FCSTD DOCUMENT  (FreeCAD 0.20R28647 (Git))
Label: assembly
License: All rights reserved
LicenseURL: http://en.wikipedia.org/wiki/All_rights_reserved
objects: App::Link×4, App::DocumentObjectGroup×3, PartDesign::CoordinateSystem×1, App::FeaturePython×1, App::Part×1
note: 1 computed .brp shape members not serialized (recipe doc carries the construction recipe); baked Part::Feature solids carry a one-line shape summary decoded from their .brp
EXTERNAL_REF file=axis.FCStd obj=LCS_Origin
EXTERNAL_REF file=axis.FCStd obj=Assembly
EXTERNAL_REF file=bearing.FCStd obj=LCS_1
EXTERNAL_REF file=bearing.FCStd obj=Assembly
EXTERNAL_REF file=bearing.FCStd obj=LCS_2
EXTERNAL_REF file=axis.FCStd obj=LCS_1

FEATURE [App::DocumentObjectGroup] Parts
FEATURE [PartDesign::CoordinateSystem] LCS_Origin
  AttacherType = Attacher::AttachEngine3D
  MapMode = 2
  Support = -> [X_Axis]
FEATURE [App::FeaturePython] Variables  # WARN: FeaturePython — macro-defined, semantics opaque (R4)
  Type = App::PropertyContainer
  pump = 10
FEATURE [App::DocumentObjectGroup] Constraints
FEATURE [App::DocumentObjectGroup] Configurations
FEATURE [App::Link] axis
  AttachedBy = #LCS_Origin
  AttachedTo = Parent Assembly#LCS_Origin
  LinkedObject = -> <external axis.FCStd>#Assembly
  SolverId = Asm4EE
  expr: Placement = LCS_Origin.Placement * AttachmentOffset * axis#LCS_Origin.Placement ^ -1
FEATURE [App::Link] bearing_1
  AttachedBy = #LCS_1
  AttachedTo = axis#LCS_Origin
  AttachmentOffset = pos=(0,0,0) rot=(0,1,0;4.71239rad)
  LinkPlacement = pos=(-4.5,0,-1e-15) rot=(0.57735,0.57735,-0.57735;4.18879rad)
  LinkedObject = -> <external bearing.FCStd>#Assembly
  Placement = pos=(-4.5,0,-1e-15) rot=(0.57735,0.57735,-0.57735;4.18879rad)
  SolverId = Asm4EE
  expr: Placement = axis.Placement * axis#LCS_Origin.Placement * AttachmentOffset * bearing#LCS_1.Placement ^ -1
FEATURE [App::Link] bearing_2
  AttachedBy = #LCS_1
  AttachedTo = bearing_1#LCS_2
  LinkPlacement = pos=(-13.5,-5e-16,-4e-15) rot=(0.57735,0.57735,-0.57735;4.18879rad)
  LinkedObject = -> <external bearing.FCStd>#Assembly
  Placement = pos=(-13.5,-5e-16,-4e-15) rot=(0.57735,0.57735,-0.57735;4.18879rad)
  SolverId = Asm4EE
  expr: Placement = bearing_1.Placement * bearing#LCS_2.Placement * AttachmentOffset * bearing#LCS_1.Placement ^ -1
FEATURE [App::Link] bearing_3
  AttachedBy = #LCS_1
  AttachedTo = axis#LCS_1
  AttachmentOffset = pos=(0,0,10) rot=(0,0,1;0rad)
  LinkPlacement = pos=(84.5,0,-3.2e-15) rot=(0.57735,-0.57735,0.57735;4.18879rad)
  LinkedObject = -> <external bearing.FCStd>#Assembly
  Placement = pos=(84.5,0,-3.2e-15) rot=(0.57735,-0.57735,0.57735;4.18879rad)
  SolverId = Asm4EE
  expr: .AttachmentOffset.Base.z = Variables.pump
  expr: Placement = axis.Placement * axis#LCS_1.Placement * AttachmentOffset * bearing#LCS_1.Placement ^ -1
FEATURE [App::Part] Assembly
  AssemblyType = Part::Link
  Group = -> [LCS_Origin,Variables,Constraints,Configurations,axis,bearing_1,bearing_2,bearing_3]
  Origin = -> Origin
  Type = Assembly

RESOLVED EXTERNAL PARTS (link-assembly join: the EXTERNAL_REF files above that resolve inside this repo's crawl, each included once):
---- part axis.FCStd = doc fcstd_0d107da27abc ----
FCSTD DOCUMENT  (FreeCAD 0.20R28647 (Git))
Label: axis
License: All rights reserved
LicenseURL: http://en.wikipedia.org/wiki/All_rights_reserved
objects: App::DocumentObjectGroup×3, PartDesign::CoordinateSystem×3, App::FeaturePython×1, Sketcher::SketchObject×1, PartDesign::Revolution×1, PartDesign::Body×1, App::Part×1
note: 7 computed .brp shape members not serialized (recipe doc carries the construction recipe); baked Part::Feature solids carry a one-line shape summary decoded from their .brp

FEATURE [App::DocumentObjectGroup] Parts
FEATURE [PartDesign::CoordinateSystem] LCS_Origin
  AttacherType = Attacher::AttachEngine3D
  MapMode = 2
  Support = -> [X_Axis]
FEATURE [App::FeaturePython] Variables  # WARN: FeaturePython — macro-defined, semantics opaque (R4)
  Type = App::PropertyContainer
FEATURE [App::DocumentObjectGroup] Constraints
FEATURE [App::DocumentObjectGroup] Configurations
FEATURE [PartDesign::CoordinateSystem] LCS_0
  AttacherType = Attacher::AttachEngine3D
  MapMode = 2
  Support = -> [X_Axis001]
FEATURE [Sketcher::SketchObject] Sketch
  FullyConstrained = true
  MapMode = 5
  Support = -> [XY_Plane001]
  sketch-geometry (10):
    g0: LineSegment StartX=-36 StartY=0 StartZ=0 EndX=-36 EndY=7.5 EndZ=0
    g1: LineSegment StartX=-36 StartY=7.5 StartZ=0 EndX=-18 EndY=7.5 EndZ=0
    g2: LineSegment StartX=-18 StartY=7.5 StartZ=0 EndX=-18 EndY=10 EndZ=0
    g3: LineSegment StartX=-18 StartY=10 StartZ=0 EndX=0 EndY=10 EndZ=0
    g4: LineSegment StartX=0 StartY=10 StartZ=0 EndX=0 EndY=12.5 EndZ=0
    g5: LineSegment StartX=0 StartY=12.5 StartZ=0 EndX=70 EndY=12.5 EndZ=0
    g6: LineSegment StartX=70 StartY=12.5 StartZ=0 EndX=70 EndY=10 EndZ=0
    g7: LineSegment StartX=70 StartY=10 StartZ=0 EndX=88 EndY=10 EndZ=0
    g8: LineSegment StartX=88 StartY=10 StartZ=0 EndX=88 EndY=0 EndZ=0
    g9: LineSegment StartX=88 StartY=0 StartZ=0 EndX=-36 EndY=0 EndZ=0
  constraints (30):
    c: PointOnObject(g0,g-1)
    c: Vertical(g0)
    c: Coincident(g0,g1)
    c: Horizontal(g1)
    c: Coincident(g1,g2)
    c: Vertical(g2)
    c: Coincident(g2,g3)
    c: PointOnObject(g3,g-2)
    c: Horizontal(g3)
    c: Coincident(g3,g4)
    c: PointOnObject(g4,g-2)
    c: Coincident(g4,g5)
    c: Horizontal(g5)
    c: Coincident(g5,g6)
    c: Vertical(g6)
    c: Coincident(g6,g7)
    c: Horizontal(g7)
    c: Coincident(g7,g8)
    c: PointOnObject(g8,g-1)
    c: Vertical(g8)
    c: Coincident(g8,g9)
    c: Coincident(g9,g0)
    c: DistanceY(g0,g0) = 7.5
    c: Horizontal(g6,g3)
    c: Equal(g7,g3)
    c: Equal(g3,g1)
    c: DistanceY(g8,g8) = 10
    c: DistanceX(g5,g5) = 70
    c: DistanceX(g3,g3) = 18
    c: DistanceY(g4) = 12.5
FEATURE [PartDesign::Revolution] Revolution
  Angle = 360
  Axis = (1,0,0)
  Base = (0,0,0)
  Profile = -> Sketch
  ReferenceAxis = -> Sketch [H_Axis]
FEATURE [PartDesign::Body] Body
  Group = -> [LCS_0,Sketch,Revolution]
  Origin = -> Origin001
  Tip = -> Revolution
FEATURE [PartDesign::CoordinateSystem] LCS_1
  AttacherType = Attacher::AttachEngine3D
  MapMode = 11
  Placement = pos=(70,0,0) rot=(0.707107,0,0.707107;3.14159rad)
  Support = -> [Revolution]
FEATURE [App::Part] Assembly
  AssemblyType = Part::Link
  Group = -> [LCS_Origin,Variables,Constraints,Configurations,LCS_1,Body]
  LabelDocUser = axis
  LabelPartUser = Assembly
  Origin = -> Origin
  ShapeVolumeUser = 25.0 mm x 25.0 mm x 87.0 mm
  Type = Assembly
---- part bearing.FCStd = doc fcstd_8ef9f0ed4e75 ----
FCSTD DOCUMENT  (FreeCAD 0.20R28647 (Git))
Label: bearing
License: All rights reserved
LicenseURL: http://en.wikipedia.org/wiki/All_rights_reserved
objects: App::DocumentObjectGroup×3, PartDesign::CoordinateSystem×3, App::FeaturePython×1, Sketcher::SketchObject×1, PartDesign::Revolution×1, PartDesign::Body×1, App::Part×1
note: 7 computed .brp shape members not serialized (recipe doc carries the construction recipe); baked Part::Feature solids carry a one-line shape summary decoded from their .brp

FEATURE [App::DocumentObjectGroup] Parts
FEATURE [PartDesign::CoordinateSystem] LCS_Origin
  AttacherType = Attacher::AttachEngine3D
  MapMode = 2
  Support = -> [X_Axis]
FEATURE [App::FeaturePython] Variables  # WARN: FeaturePython — macro-defined, semantics opaque (R4)
  Type = App::PropertyContainer
FEATURE [App::DocumentObjectGroup] Constraints
FEATURE [App::DocumentObjectGroup] Configurations
FEATURE [Sketcher::SketchObject] Sketch
  FullyConstrained = true
  MapMode = 5
  Placement = pos=(0,0,0) rot=(1,0,0;1.5708rad)
  Support = -> [XZ_Plane001]
  sketch-geometry (22):
    g0: LineSegment StartX=-18.5 StartY=4.14645 StartZ=0 EndX=-18.5 EndY=-4.14645 EndZ=0
    g1: LineSegment StartX=-18.5 StartY=-4.14645 StartZ=0 EndX=-18.1464 EndY=-4.5 EndZ=0
    g2: LineSegment StartX=-18.1464 StartY=-4.5 StartZ=0 EndX=-16.2 EndY=-4.5 EndZ=0
    g3: LineSegment StartX=-16.2 StartY=-4.5 StartZ=0 EndX=-16.2 EndY=-4.2 EndZ=0
    g4: LineSegment StartX=-15.4 StartY=-4.3 StartZ=0 EndX=-12.4 EndY=-4.3 EndZ=0
    g5: LineSegment StartX=-12.4 StartY=-4.3 StartZ=0 EndX=-12.3 EndY=-4.2 EndZ=0
    g6: LineSegment StartX=-12.3 StartY=-4.2 StartZ=0 EndX=-12.3 EndY=-4.5 EndZ=0
    g7: LineSegment StartX=-12.3 StartY=-4.5 StartZ=0 EndX=-10.3536 EndY=-4.5 EndZ=0
    g8: LineSegment StartX=-10.3536 StartY=-4.5 StartZ=0 EndX=-10 EndY=-4.14645 EndZ=0
    g9: LineSegment StartX=-10 StartY=-4.14645 StartZ=0 EndX=-10 EndY=4.14645 EndZ=0
    g10: LineSegment StartX=-10 StartY=4.14645 StartZ=0 EndX=-10.3536 EndY=4.5 EndZ=0
    g11: LineSegment StartX=-10.3536 StartY=4.5 StartZ=0 EndX=-12.3 EndY=4.5 EndZ=0
    g12: LineSegment StartX=-12.3 StartY=4.5 StartZ=0 EndX=-12.3 EndY=4.2 EndZ=0
    g13: LineSegment StartX=-12.3 StartY=4.2 StartZ=0 EndX=-12.4 EndY=4.3 EndZ=0
    g14: LineSegment StartX=-12.4 StartY=4.3 StartZ=0 EndX=-15.4 EndY=4.3 EndZ=0
    g15: LineSegment StartX=-15.4 StartY=4.3 StartZ=0 EndX=-15.5 EndY=4.2 EndZ=0
    g16: LineSegment StartX=-15.5 StartY=4.2 StartZ=0 EndX=-16.2 EndY=4.2 EndZ=0
    g17: LineSegment StartX=-16.2 StartY=4.2 StartZ=0 EndX=-16.2 EndY=4.5 EndZ=0
    g18: LineSegment StartX=-16.2 StartY=4.5 StartZ=0 EndX=-18.1464 EndY=4.5 EndZ=0
    g19: LineSegment StartX=-18.1464 StartY=4.5 StartZ=0 EndX=-18.5 EndY=4.14645 EndZ=0
    g20: LineSegment StartX=-15.4 StartY=-4.3 StartZ=0 EndX=-15.5 EndY=-4.2 EndZ=0
    g21: LineSegment StartX=-15.5 StartY=-4.2 StartZ=0 EndX=-16.2 EndY=-4.2 EndZ=0
  constraints (61):
    c: Vertical(g0)
    c: Coincident(g0,g1)
    c: Coincident(g1,g2)
    c: Horizontal(g2)
    c: Coincident(g2,g3)
    c: Coincident(g4,g5)
    c: Coincident(g5,g6)
    c: Coincident(g6,g7)
    c: Coincident(g7,g8)
    c: Coincident(g8,g9)
    c: Coincident(g9,g10)
    c: Coincident(g10,g11)
    c: Horizontal(g11)
    c: Coincident(g11,g12)
    c: Vertical(g12)
    c: Coincident(g12,g13)
    c: Coincident(g13,g14)
    c: Horizontal(g14)
    c: Coincident(g14,g15)
    c: Coincident(g15,g16)
    c: Horizontal(g16)
    c: Coincident(g16,g17)
    c: Vertical(g17)
    c: Coincident(g17,g18)
    c: Horizontal(g18)
    c: Coincident(g18,g19)
    c: Coincident(g19,g0)
    c: Coincident(g4,g20)
    c: Coincident(g20,g21)
    c: Coincident(g21,g3)
    c: Vertical(g3)
    c: Horizontal(g21)
    c: Horizontal(g4)
    c: Vertical(g6)
    c: Horizontal(g7)
    c: Horizontal(g11,g17)
    c: Symmetric(g8,g9,g-1)
    c: Symmetric(g10,g7,g-1)
    c: Equal(g7,g11)
    c: Symmetric(g13,g4,g-1)
    c: Equal(g6,g12)
    c: Angle(g8) = 0.785398
    c: Parallel(g8,g19)
    c: Parallel(g15,g5)
    c: Parallel(g5,g8)
    c: Parallel(g13,g20)
    c: Parallel(g20,g1)
    c: Equal(g2,g18)
    c: Symmetric(g20,g15,g-1)
    c: Equal(g12,g17)
    c: Symmetric(g18,g1,g-1)
    c: DistanceY(g7,g10) = 9
    c: DistanceX(g8) = -10
    c: Distance(g8) = 0.5
    c: DistanceY(g6,g4) = 0.2
    c: Equal(g1,g8)
    c: Equal(g7,g2)
    c: DistanceY(g6,g6) = 0.3
    c: DistanceX(g0) = -18.5
    c: DistanceX(g4,g4) = 3
    c: DistanceX(g21,g21) = 0.7
FEATURE [PartDesign::Revolution] Revolution
  Angle = 360
  Axis = (0,-2e-16,1)
  Base = (0,0,0)
  Placement = pos=(0,0,0) rot=(1,0,0;1.5708rad)
  Profile = -> Sketch
  ReferenceAxis = -> Sketch [V_Axis]
FEATURE [PartDesign::Body] Body  label="BallBearing 37x20x9"
  Group = -> [Sketch,Revolution]
  Origin = -> Origin001
  Tip = -> Revolution
FEATURE [PartDesign::CoordinateSystem] LCS_1
  AttacherType = Attacher::AttachEngine3D
  MapMode = 11
  Placement = pos=(0,-1e-15,-4.5) rot=(0,0,-1;1.5708rad)
  Support = -> [Revolution]
FEATURE [PartDesign::CoordinateSystem] LCS_2
  AttacherType = Attacher::AttachEngine3D
  MapMode = 11
  Placement = pos=(0,1e-15,4.5) rot=(0,0,-1;1.5708rad)
  Support = -> [Revolution]
FEATURE [App::Part] Assembly  label="asm_Bearing 37x20x9"
  AssemblyType = Part::Link
  Group = -> [LCS_Origin,Variables,Constraints,Configurations,Body,LCS_1,LCS_2]
  LabelDocUser = bearing
  LabelPartUser = asm_Bearing 37x20x9
  Origin = -> Origin
  ShapeVolumeUser = 9.0 mm x 37.0 mm x 37.0 mm
  Type = Assembly
